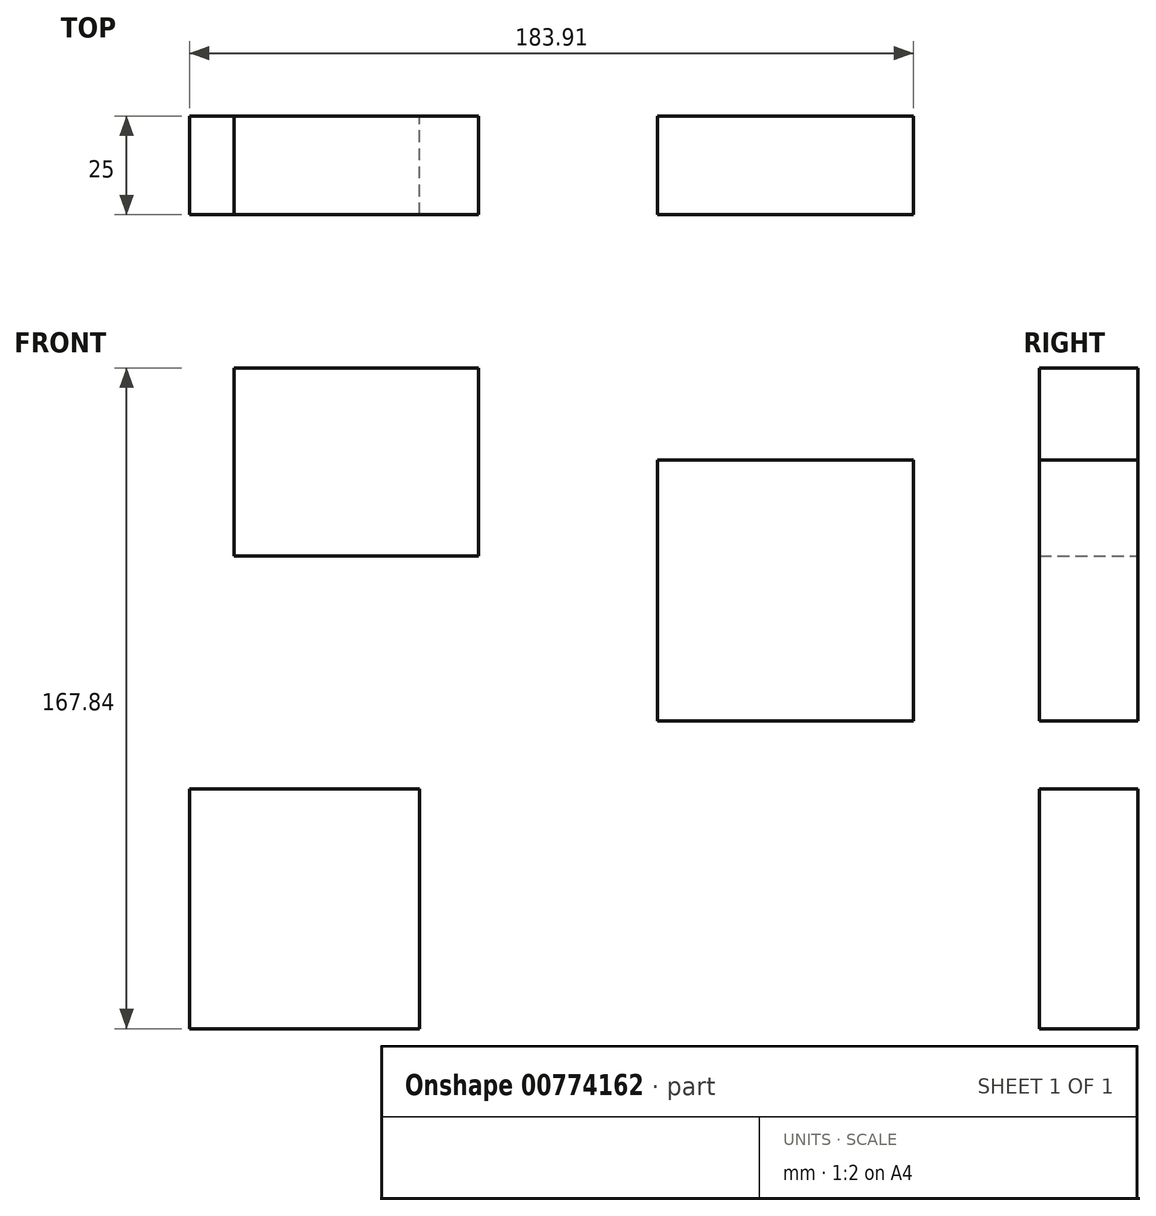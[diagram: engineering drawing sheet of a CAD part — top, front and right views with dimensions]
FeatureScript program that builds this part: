
annotation { "Feature Type Name" : "Feature", "Feature Type Description" : "" }
export const myFeature = defineFeature(function(context is Context, id is Id, definition is map)
    precondition{}
    {
        {
            var Q0;
            Q0=qCreatedBy(makeId("Front.planeOp"),FACE);
            var sketch = newSketch(context, id + "F0", { "sketchPlane" : qUnion([Q0])});
            skLineSegment(sketch, "E0.bottom", {"start": v(-150.7, 47.79) * mm, "end": v(-88.62, 47.79) * mm});
            skLineSegment(sketch, "E0.top", {"start": v(-150.7, 0) * mm, "end": v(-88.62, 0) * mm});
            skLineSegment(sketch, "E0.left", {"start": v(-150.7, 47.79) * mm, "end": v(-150.7, 0) * mm});
            skLineSegment(sketch, "E0.right", {"start": v(-88.62, 47.79) * mm, "end": v(-88.62, 0) * mm});
            skLineSegment(sketch, "E1.bottom", {"start": v(-43.23, 24.4) * mm, "end": v(21.86, 24.4) * mm});
            skLineSegment(sketch, "E1.top", {"start": v(-43.23, -41.92) * mm, "end": v(21.86, -41.92) * mm});
            skLineSegment(sketch, "E1.left", {"start": v(-43.23, 24.4) * mm, "end": v(-43.23, -41.92) * mm});
            skLineSegment(sketch, "E1.right", {"start": v(21.86, 24.4) * mm, "end": v(21.86, -41.92) * mm});
            skLineSegment(sketch, "E2.bottom", {"start": v(-103.64, -59.12) * mm, "end": v(-162.05, -59.12) * mm});
            skLineSegment(sketch, "E2.top", {"start": v(-103.64, -120.05) * mm, "end": v(-162.05, -120.05) * mm});
            skLineSegment(sketch, "E2.left", {"start": v(-103.64, -59.12) * mm, "end": v(-103.64, -120.05) * mm});
            skLineSegment(sketch, "E2.right", {"start": v(-162.05, -59.12) * mm, "end": v(-162.05, -120.05) * mm});
            skSolve(sketch);
        }
        {
            var Q0;
            Q0 = qSketchRegion(id + "F0", true);
            extrude(context, id + "F1", {"entities" : qUnion([Q0]), "depth" : 25 * mm, "offsetDistance" : 25 * mm});
        }
    });
